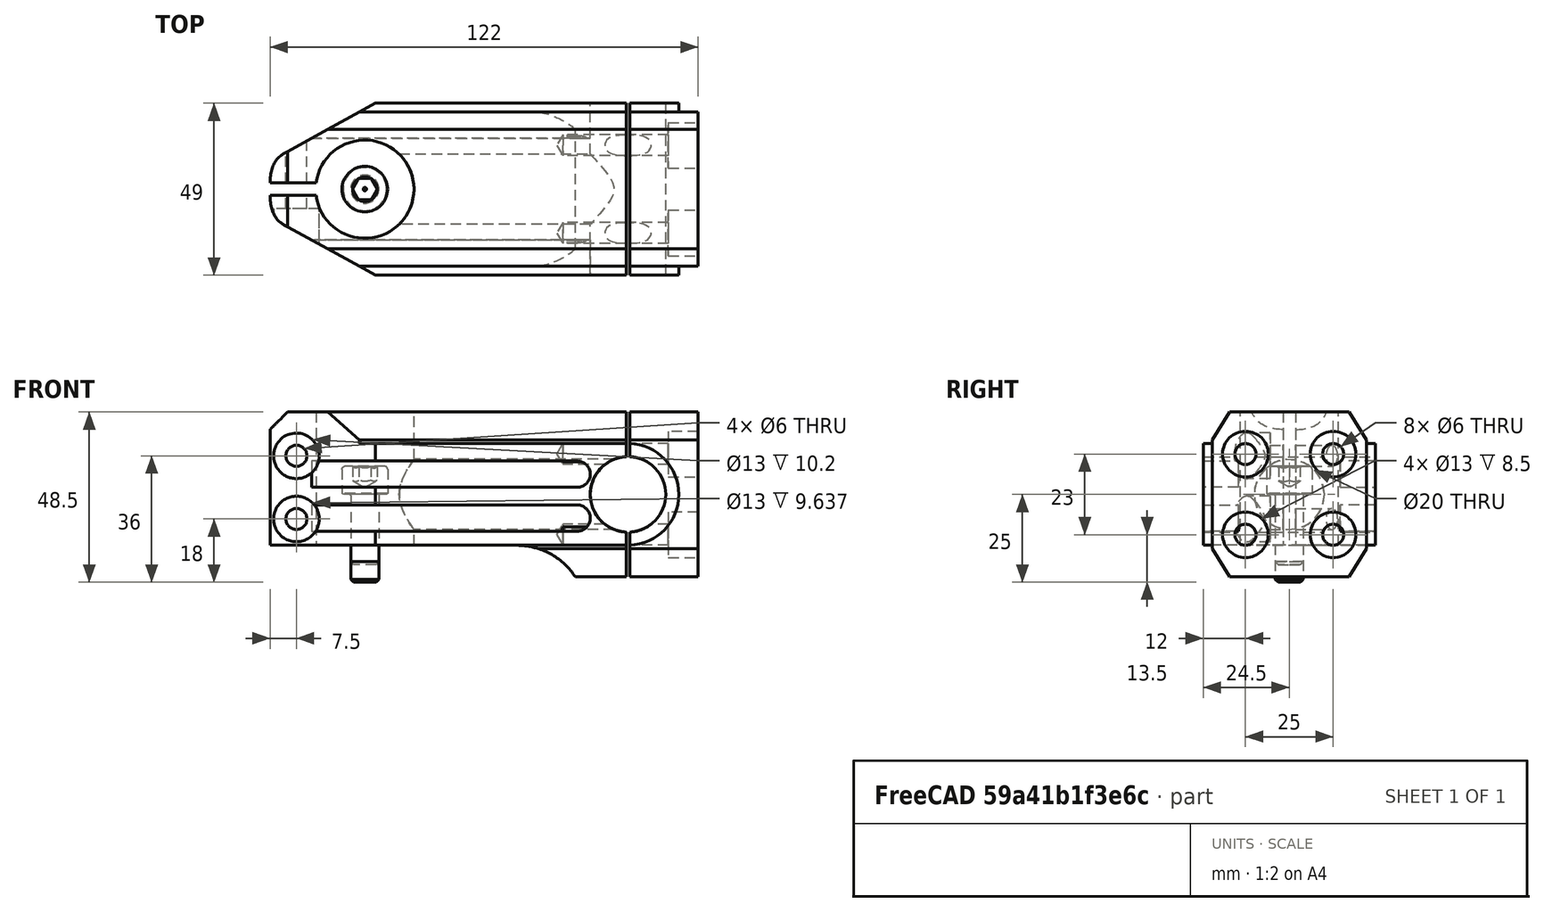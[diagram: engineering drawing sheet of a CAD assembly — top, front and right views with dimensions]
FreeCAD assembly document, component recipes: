
FREECAD ASSEMBLY — COMPONENT RECIPES ("Anchor")

This assembly document has 7 components, labeled P0..P6 below (a component is one placed body or linked part). 1 of them carries a construction recipe — the FreeCAD feature program that regenerates the part from scratch, quoted from this document or its linked companion documents; the rest are supplied as boundary geometry only. No exploded tour is included for this assembly.
COMPONENT P0 — geometry summary ("M8x20-Screw001"; no construction recipe available for this part):
  bounding box: 28.0 x 13.0 x 13.0 mm
  tessellated surface: 13,622 triangles
  volume: 1899 mm^3 (40% of its bounding box)
  symmetry: 6-fold rotationally symmetric about the y axis; mirror-symmetric across its x mid-plane, z mid-plane
COMPONENT P1 — geometry summary ("M8x20-Screw002"; no construction recipe available for this part):
  bounding box: 28.0 x 13.0 x 13.0 mm
  tessellated surface: 13,622 triangles
  volume: 1899 mm^3 (40% of its bounding box)
  symmetry: 6-fold rotationally symmetric about the y axis; mirror-symmetric across its x mid-plane, z mid-plane
COMPONENT P2 — geometry summary ("M8x25-Screw001"; no construction recipe available for this part):
  bounding box: 33.0 x 13.0 x 13.0 mm
  tessellated surface: 13,622 triangles
  volume: 2150 mm^3 (39% of its bounding box)
  symmetry: 6-fold rotationally symmetric about the x axis; mirror-symmetric across its y mid-plane, z mid-plane
COMPONENT P3 — geometry summary ("M8x25-Screw002"; no construction recipe available for this part):
  bounding box: 33.0 x 13.0 x 13.0 mm
  tessellated surface: 13,622 triangles
  volume: 2150 mm^3 (39% of its bounding box)
  symmetry: 6-fold rotationally symmetric about the x axis; mirror-symmetric across its y mid-plane, z mid-plane
COMPONENT P4 — geometry summary ("M8x25-Screw003"; no construction recipe available for this part):
  bounding box: 33.0 x 13.0 x 13.0 mm
  tessellated surface: 13,622 triangles
  volume: 2150 mm^3 (39% of its bounding box)
  symmetry: 6-fold rotationally symmetric about the x axis; mirror-symmetric across its y mid-plane, z mid-plane
COMPONENT P5 — geometry summary ("M8x25-Screw004"; no construction recipe available for this part):
  bounding box: 33.0 x 13.0 x 13.0 mm
  tessellated surface: 13,622 triangles
  volume: 2150 mm^3 (39% of its bounding box)
  symmetry: 6-fold rotationally symmetric about the x axis; mirror-symmetric across its y mid-plane, z mid-plane
COMPONENT P6 — recipe-attached ("Stem001", modeled in this document).
Construction recipe (the document's own serialized feature program — sketch geometry with constraints, then the solid features built on it; lengths are millimeters unless a unit is written):

FEATURE [Sketcher::SketchObject] Sketch
  ArcFitTolerance = 1e-06
  AttachmentSupport = -> [XZ_Plane001]
  FullyConstrained = true
  MakeInternals = false
  MapMode = 5
  Placement = pos=(0,0,0) rot=(1,0,0;1.5708rad)
  expr: Constraints[15] = <<VarSet>>.Size
  expr: Constraints[16] = <<VarSet>>.Size + 20 mm
  sketch-geometry (7):
    g0: Circle CenterX=75 CenterY=0 CenterZ=0 NormalX=0 NormalY=0 NormalZ=1 AngleXU=0 Radius=10.75
    g1: LineSegment StartX=0 StartY=23.5 StartZ=0 EndX=95 EndY=23.5 EndZ=0
    g2: LineSegment StartX=95 StartY=23.5 StartZ=0 EndX=95 EndY=-23.5 EndZ=0
    g3: LineSegment StartX=95 StartY=-23.5 StartZ=0 EndX=0 EndY=-23.5 EndZ=0
    g4: LineSegment StartX=0 StartY=-23.5 StartZ=0 EndX=-27 EndY=-23.5 EndZ=0
    g5: LineSegment StartX=-27 StartY=-23.5 StartZ=0 EndX=-27 EndY=23.5 EndZ=0
    g6: LineSegment StartX=-27 StartY=23.5 StartZ=0 EndX=0 EndY=23.5 EndZ=0
  constraints (20):
    c: Diameter(g0) = 21.5
    c: PointOnObject(g0,g-1)
    c: PointOnObject(g1,g-2)
    c: Horizontal(g1)
    c: Coincident(g1,g2)
    c: Coincident(g2,g3)
    c: PointOnObject(g3,g-2)
    c: Horizontal(g3)
    c: Coincident(g3,g4)
    c: Horizontal(g4)
    c: Coincident(g4,g5)
    c: Vertical(g5)
    c: Coincident(g5,g6)
    c: Coincident(g6,g1)
    c: Parallel(g6,g-1)
    c: Distance(g0,g-1) = 75
    c: Distance(g1) = 95
    c: Distance(g2) = 47
    c: Distance(g4) = 27
    c: Symmetric(g1,g2,g-1)
FEATURE [PartDesign::Pad] Pad
  Direction = (0,-1,2e-16)
  Length = 22
  Length2 = 10
  Placement = pos=(0,0,0) rot=(1,0,0;1.5708rad)
  Profile = -> Sketch
  ReferenceAxis = -> Sketch [N_Axis]
  Refine = true
  Suppressed = false
  Type = 0
FEATURE [PartDesign::Chamfer] Chamfer
  Angle = 45
  Base = -> Pad [Edge14,Edge15]
  BaseFeature = -> Pad
  ChamferType = 1
  FlipDirection = false
  Placement = pos=(0,0,0) rot=(1,0,0;1.5708rad)
  Refine = true
  Size = 8
  Size2 = 5
  SupportTransform = false
  Suppressed = false
  UseAllEdges = false
FEATURE [Sketcher::SketchObject] Sketch001
  ArcFitTolerance = 1e-06
  AttachmentSupport = -> [Chamfer]
  ExternalGeometry = -> [Chamfer]
  FullyConstrained = true
  MakeInternals = false
  MapMode = 5
  Placement = pos=(0,-22,0) rot=(1,0,0;1.5708rad)
  sketch-geometry (5):
    g0: ArcOfCircle CenterX=75 CenterY=4.9e-15 CenterZ=0 NormalX=0 NormalY=0 NormalZ=1 AngleXU=0 Radius=14.5 StartAngle=4.71239 EndAngle=7.85398
    g1: LineSegment StartX=75 StartY=14.5 StartZ=0 EndX=-27 EndY=14.5 EndZ=0
    g2: LineSegment StartX=75 StartY=-14.5 StartZ=0 EndX=-27 EndY=-14.5 EndZ=0
    g3: LineSegment StartX=-27 StartY=14.5 StartZ=0 EndX=-27 EndY=-14.5 EndZ=0
    g4: Circle CenterX=75 CenterY=4.9e-15 CenterZ=0 NormalX=0 NormalY=0 NormalZ=1 AngleXU=0 Radius=10.75
  constraints (14):
    c: Coincident(g0,g-4)
    c: Vertical(g0,g0)
    c: Vertical(g0,g0)
    c: Coincident(g0,g1)
    c: Coincident(g0,g2)
    c: Horizontal(g1)
    c: Horizontal(g2)
    c: Radius(g0) = 14.5
    c: Vertical(g3)
    c: Coincident(g1,g3)
    c: Coincident(g2,g3)
    c: Distance(g-1,g3) = 27
    c: Coincident(g4,g0)
    c: Equal(g4,g-4)
FEATURE [PartDesign::Pad] Pad001
  BaseFeature = -> Chamfer
  Direction = (0,-1,2e-16)
  Length = 2.5
  Length2 = 10
  Placement = pos=(0,0,0) rot=(1,0,0;1.5708rad)
  Profile = -> Sketch001
  ReferenceAxis = -> Sketch001 [N_Axis]
  Refine = true
  Suppressed = false
  Type = 0
FEATURE [Sketcher::SketchObject] Sketch002
  ArcFitTolerance = 1e-06
  AttachmentSupport = -> [Pad001]
  ExternalGeometry = -> [Pad001]
  FullyConstrained = true
  MakeInternals = false
  MapMode = 5
  Placement = pos=(0,-24.5,6.1e-15) rot=(1,0,0;1.5708rad)
  expr: Constraints[18] = VarSet.Size - 14.5 mm
  sketch-geometry (8):
    g0: LineSegment StartX=-27 StartY=9.5 StartZ=0 EndX=-27 EndY=2 EndZ=0
    g1: LineSegment StartX=-27 StartY=2 StartZ=0 EndX=60.5 EndY=2 EndZ=0
    g2: LineSegment StartX=60.5 StartY=9.5 StartZ=0 EndX=-27 EndY=9.5 EndZ=0
    g3: LineSegment StartX=-27 StartY=-3 StartZ=0 EndX=-27 EndY=-10.5 EndZ=0
    g4: LineSegment StartX=-27 StartY=-10.5 StartZ=0 EndX=60.5 EndY=-10.5 EndZ=0
    g5: LineSegment StartX=60.5 StartY=-3 StartZ=0 EndX=-27 EndY=-3 EndZ=0
    g6: ArcOfCircle CenterX=60.5 CenterY=5.75 CenterZ=0 NormalX=0 NormalY=0 NormalZ=1 AngleXU=0 Radius=3.75 StartAngle=4.71239 EndAngle=7.85398
    g7: ArcOfCircle CenterX=60.5 CenterY=-6.75 CenterZ=0 NormalX=0 NormalY=0 NormalZ=1 AngleXU=0 Radius=3.75 StartAngle=4.71239 EndAngle=7.85398
  constraints (22):
    c: Coincident(g0,g1)
    c: Coincident(g2,g0)
    c: Vertical(g0)
    c: Horizontal(g1)
    c: Horizontal(g2)
    c: PointOnObject(g0,g-3)
    c: Coincident(g3,g4)
    c: Coincident(g5,g3)
    c: Vertical(g3)
    c: Horizontal(g4)
    c: Horizontal(g5)
    c: PointOnObject(g3,g-3)
    c: Tangent(g6,g2) = -1.5708
    c: Tangent(g6,g1) = -1.5708
    c: Tangent(g7,g5) = -1.5708
    c: Tangent(g7,g4) = -1.5708
    c: Distance(g1,g2) = 7.5
    c: Distance(g-1,g1) = 2
    c: Distance(g6,g-2) = 60.5
    c: Vertical(g6,g7)
    c: Equal(g3,g0)
    c: Distance(g-1,g5) = 3
FEATURE [PartDesign::Pocket] Pocket
  BaseFeature = -> Pad001
  Direction = (0,1,-2e-16)
  Length = 10
  Length2 = 5
  Placement = pos=(0,0,0) rot=(1,0,0;1.5708rad)
  Profile = -> Sketch002
  ReferenceAxis = -> Sketch002 [N_Axis]
  Refine = true
  Suppressed = false
  Type = 0
FEATURE [Sketcher::SketchObject] Sketch003
  ArcFitTolerance = 1e-06
  AttachmentSupport = -> [Pocket]
  ExternalGeometry = -> [Pocket]
  FullyConstrained = true
  MakeInternals = false
  MapMode = 5
  Placement = pos=(0,-22,0) rot=(1,0,0;1.5708rad)
  expr: Constraints[9] = VarSet.Size - 15 mm
  sketch-geometry (5):
    g0: LineSegment StartX=43.2967 StartY=-14.5 StartZ=0 EndX=-27 EndY=-14.5 EndZ=0
    g1: LineSegment StartX=-27 StartY=-14.5 StartZ=0 EndX=-27 EndY=-23.5 EndZ=0
    g2: LineSegment StartX=-27 StartY=-23.5 StartZ=0 EndX=0 EndY=-23.5 EndZ=0
    g3: LineSegment StartX=0 StartY=-23.5 StartZ=0 EndX=60 EndY=-23.5 EndZ=0
    g4: ArcOfCircle CenterX=43.2967 CenterY=-34.5 CenterZ=0 NormalX=0 NormalY=0 NormalZ=1 AngleXU=0 Radius=20 StartAngle=0.582364 EndAngle=1.5708
  constraints (13):
    c: PointOnObject(g0,g-5)
    c: Coincident(g0,g-5)
    c: Coincident(g0,g1)
    c: Coincident(g1,g-4)
    c: Coincident(g1,g2)
    c: PointOnObject(g2,g-3)
    c: Coincident(g2,g3)
    c: PointOnObject(g3,g-3)
    c: PointOnObject(g2,g-2)
    c: DistanceX(g3,g3) = 60
    c: Coincident(g3,g4)
    c: Tangent(g4,g0) = -1.5708
    c: Radius(g4) = 20
FEATURE [PartDesign::Pocket] Pocket001
  BaseFeature = -> Pocket
  Direction = (0,1,-2e-16)
  Length = 5
  Length2 = 5
  Placement = pos=(0,0,0) rot=(1,0,0;1.5708rad)
  Profile = -> Sketch003
  ReferenceAxis = -> Sketch003 [N_Axis]
  Refine = true
  Suppressed = false
  Type = 1
FEATURE [Sketcher::SketchObject] Sketch004
  ArcFitTolerance = 1e-06
  AttachmentSupport = -> [Pocket001]
  ExternalGeometry = -> [Pocket001]
  FullyConstrained = true
  MakeInternals = false
  MapMode = 5
  Placement = pos=(0,1.13e-14,23.5) rot=(0,0,1;3.14159rad)
  sketch-geometry (10):
    g0: LineSegment StartX=-3 StartY=24.5 StartZ=0 EndX=27 EndY=24.5 EndZ=0
    g1: LineSegment StartX=27 StartY=24.5 StartZ=0 EndX=27 EndY=1.75 EndZ=0
    g2: LineSegment StartX=-3 StartY=24.5 StartZ=0 EndX=23 EndY=10.2 EndZ=0
    g3: LineSegment [constr] StartX=23 StartY=10.2 StartZ=0 EndX=27 EndY=8 EndZ=0
    g4: Circle [constr] CenterX=23 CenterY=10.2 CenterZ=0 NormalX=0 NormalY=0 NormalZ=1 AngleXU=0 Radius=1
    g5: Circle [constr] CenterX=27 CenterY=8 CenterZ=0 NormalX=0 NormalY=0 NormalZ=1 AngleXU=0 Radius=1
    g6: Circle [constr] CenterX=27 CenterY=1.75 CenterZ=0 NormalX=0 NormalY=0 NormalZ=1 AngleXU=0 Radius=1
    g7: BSplineCurve PolesCount=3 KnotsCount=2 Degree=2 IsPeriodic=0
    g8: GeomPoint [constr] X=23 Y=10.2 Z=0
    g9: GeomPoint [constr] X=27 Y=1.75 Z=0
  constraints (23):
    c: PointOnObject(g0,g-3)
    c: Coincident(g0,g-4)
    c: Coincident(g0,g1)
    c: PointOnObject(g1,g-6)
    c: DistanceY(g-6,g1) = 1.75
    c: Distance(g0,g-2) = 3
    c: Coincident(g0,g2)
    c: Distance(g2,g-2) = 23
    c: Coincident(g3,g2)
    c: PointOnObject(g3,g1)
    c: Parallel(g3,g2)
    c: DistanceY(g-6,g3) = 8
    c: Weight(g4) = 1
    c: Equal(g4,g5)
    c: Equal(g4,g6)
    c: InternalAlignment(g4,g7)
    c: InternalAlignment(g5,g7)
    c: InternalAlignment(g6,g7)
    c: InternalAlignment(g8,g7)
    c: InternalAlignment(g9,g7)
    c: Coincident(g4,g2)
    c: Coincident(g6,g1)
    c: Coincident(g5,g3)
FEATURE [PartDesign::Pocket] Pocket002
  BaseFeature = -> Pocket001
  Direction = (0,0,-1)
  Length = 5
  Length2 = 5
  Placement = pos=(0,0,0) rot=(1,0,0;1.5708rad)
  Profile = -> Sketch004
  ReferenceAxis = -> Sketch004 [N_Axis]
  Refine = true
  Suppressed = false
  Type = 1
FEATURE [PartDesign::Mirrored] Mirrored
  BaseFeature = -> Pocket002
  MirrorPlane = -> XZ_Plane001
  Placement = pos=(0,0,0) rot=(1,0,0;1.5708rad)
  Refine = true
  Suppressed = false
  TransformMode = 1
FEATURE [Sketcher::SketchObject] Sketch005
  ArcFitTolerance = 1e-06
  AttachmentSupport = -> [Mirrored]
  ExternalGeometry = -> [Mirrored]
  FullyConstrained = true
  MakeInternals = false
  MapMode = 5
  Placement = pos=(0,0,23.5) rot=(0,0,1;3.14159rad)
  sketch-geometry (4):
    g0: ArcOfCircle CenterX=0 CenterY=0 CenterZ=0 NormalX=0 NormalY=0 NormalZ=1 AngleXU=0 Radius=14 StartAngle=0.125328 EndAngle=6.15786
    g1: LineSegment StartX=27 StartY=1.75 StartZ=0 EndX=13.8902 EndY=1.75 EndZ=0
    g2: LineSegment StartX=27 StartY=-1.75 StartZ=0 EndX=13.8902 EndY=-1.75 EndZ=0
    g3: LineSegment StartX=27 StartY=1.75 StartZ=0 EndX=27 EndY=-1.75 EndZ=0
  constraints (10):
    c: Diameter(g0) = 28
    c: Coincident(g0,g-1)
    c: Coincident(g1,g-3)
    c: Horizontal(g1)
    c: Coincident(g2,g-3)
    c: Horizontal(g2)
    c: Coincident(g3,g1)
    c: Coincident(g3,g2)
    c: Coincident(g0,g2)
    c: Coincident(g0,g1)
FEATURE [PartDesign::Pocket] Pocket003
  BaseFeature = -> Mirrored
  Direction = (0,0,-1)
  Length = 5
  Length2 = 5
  Placement = pos=(0,0,0) rot=(1,0,0;1.5708rad)
  Profile = -> Sketch005
  ReferenceAxis = -> Sketch005 [N_Axis]
  Refine = true
  Suppressed = false
  Type = 1
FEATURE [Sketcher::SketchObject] Sketch006
  ArcFitTolerance = 1e-06
  AttachmentSupport = -> [XZ_Plane001]
  ExternalGeometry = -> [Pocket003]
  FullyConstrained = true
  MakeInternals = false
  MapMode = 5
  Placement = pos=(0,0,0) rot=(1,0,0;1.5708rad)
  sketch-geometry (3):
    g0: LineSegment StartX=-27 StartY=23.5 StartZ=0 EndX=-22 EndY=23.5 EndZ=0
    g1: LineSegment StartX=-22 StartY=23.5 StartZ=0 EndX=-27 EndY=18.5 EndZ=0
    g2: LineSegment StartX=-27 StartY=18.5 StartZ=0 EndX=-27 EndY=23.5 EndZ=0
  constraints (8):
    c: Coincident(g0,g-4)
    c: PointOnObject(g0,g-5)
    c: Coincident(g0,g1)
    c: PointOnObject(g1,g-3)
    c: Coincident(g1,g2)
    c: Coincident(g2,g0)
    c: DistanceX(g0,g0) = 5
    c: DistanceY(g2,g2) = 5
FEATURE [PartDesign::Pocket] Pocket004
  BaseFeature = -> Pocket003
  Direction = (0,1,-2e-16)
  Length = 5
  Length2 = 5
  Midplane = true
  Placement = pos=(0,0,0) rot=(1,0,0;1.5708rad)
  Profile = -> Sketch006
  ReferenceAxis = -> Sketch006 [N_Axis]
  Refine = true
  Suppressed = false
  Type = 1
FEATURE [Sketcher::SketchObject] Sketch007
  ArcFitTolerance = 1e-06
  AttachmentSupport = -> [Pocket004]
  FullyConstrained = true
  MakeInternals = false
  MapMode = 5
  Placement = pos=(95,0,0) rot=(0.707107,0,0.707107;3.14159rad)
  sketch-geometry (4):
    g0: Circle CenterX=11.5 CenterY=12.5 CenterZ=0 NormalX=0 NormalY=0 NormalZ=1 AngleXU=0 Radius=6.5
    g1: Circle CenterX=-11.5 CenterY=12.5 CenterZ=0 NormalX=0 NormalY=0 NormalZ=1 AngleXU=0 Radius=6.5
    g2: Circle CenterX=-11.5 CenterY=-12.5 CenterZ=0 NormalX=0 NormalY=0 NormalZ=1 AngleXU=0 Radius=6.5
    g3: Circle CenterX=11.5 CenterY=-12.5 CenterZ=0 NormalX=0 NormalY=0 NormalZ=1 AngleXU=0 Radius=6.5
  constraints (9):
    c: Symmetric(g0,g3,g-1)
    c: Symmetric(g1,g2,g-1)
    c: Symmetric(g2,g3,g-2)
    c: DistanceX(g1,g0) = 23
    c: DistanceY(g3,g0) = 25
    c: Equal(g0,g1)
    c: Equal(g1,g2)
    c: Equal(g2,g3)
    c: Diameter(g0) = 13
FEATURE [PartDesign::Pocket] Pocket005
  BaseFeature = -> Pocket004
  Direction = (-1,0,2e-16)
  Length = 8.5
  Length2 = 5
  Placement = pos=(0,0,0) rot=(1,0,0;1.5708rad)
  Profile = -> Sketch007
  ReferenceAxis = -> Sketch007 [N_Axis]
  Refine = true
  Suppressed = false
  Type = 0
FEATURE [PartDesign::Hole] Hole
  BaseFeature = -> Pocket005
  CustomThreadClearance = 0
  Depth = 30
  DepthType = 0
  Diameter = 6
  DrillForDepth = false
  DrillPoint = 1
  DrillPointAngle = 118
  HoleCutCountersinkAngle = 90
  HoleCutCustomValues = false
  HoleCutDepth = 0
  HoleCutDiameter = 6.1
  HoleCutType = 0
  ModelThread = false
  Placement = pos=(0,0,0) rot=(1,0,0;1.5708rad)
  Profile = -> Pocket005 [Face49,Face47,Face46,Face48]
  Refine = true
  Suppressed = false
  Tapered = false
  TaperedAngle = 90
  ThreadClass = 0
  ThreadDepth = 30
  ThreadDepthType = 0
  ThreadDirection = 0
  ThreadFit = 0
  ThreadSize = 0
  ThreadType = 0
  Threaded = false
  UseCustomThreadClearance = false
FEATURE [Sketcher::SketchObject] Sketch008
  ArcFitTolerance = 1e-06
  AttachmentSupport = -> [Hole]
  FullyConstrained = true
  MakeInternals = false
  MapMode = 5
  Placement = pos=(0,-14.5,4.8e-15) rot=(1,0,0;1.5708rad)
  sketch-geometry (2):
    g0: Circle CenterX=-19.5 CenterY=11 CenterZ=0 NormalX=0 NormalY=0 NormalZ=1 AngleXU=0 Radius=6.5
    g1: Circle CenterX=-19.5 CenterY=-7 CenterZ=0 NormalX=0 NormalY=0 NormalZ=1 AngleXU=0 Radius=6.5
  constraints (6):
    c: Vertical(g0,g1)
    c: Equal(g1,g0)
    c: DistanceY(g1,g-1) = 7
    c: Distance(g0,g-1) = 11
    c: DistanceX(g0,g-1) = 19.5
    c: Diameter(g0) = 13
FEATURE [PartDesign::Pocket] Pocket006
  BaseFeature = -> Hole
  Direction = (0,1,-2e-16)
  Length = 9
  Length2 = 7
  Placement = pos=(0,0,0) rot=(1,0,0;1.5708rad)
  Profile = -> Sketch008
  ReferenceAxis = -> Sketch008 [N_Axis]
  Refine = true
  Suppressed = false
  Type = 4
FEATURE [PartDesign::Hole] Hole001
  BaseFeature = -> Pocket006
  CustomThreadClearance = 0
  Depth = 25
  DepthType = 0
  Diameter = 6
  DrillForDepth = false
  DrillPoint = 1
  DrillPointAngle = 118
  HoleCutCountersinkAngle = 90
  HoleCutCustomValues = false
  HoleCutDepth = 0
  HoleCutDiameter = 6.1
  HoleCutType = 0
  ModelThread = false
  Placement = pos=(0,0,0) rot=(1,0,0;1.5708rad)
  Profile = -> Pocket006 [Face33,Face57]
  Refine = true
  Suppressed = false
  Tapered = false
  TaperedAngle = 90
  ThreadClass = 0
  ThreadDepth = 25
  ThreadDepthType = 0
  ThreadDirection = 0
  ThreadFit = 0
  ThreadSize = 0
  ThreadType = 0
  Threaded = false
  UseCustomThreadClearance = false
FEATURE [Sketcher::SketchObject] Sketch009
  ArcFitTolerance = 1e-06
  AttachmentSupport = -> [XZ_Plane001]
  ExternalGeometry = -> [Hole001]
  FullyConstrained = true
  MakeInternals = false
  MapMode = 5
  Placement = pos=(0,0,0) rot=(1,0,0;1.5708rad)
  expr: Constraints[10] = VarSet.Size + 0.5 mm
  expr: Constraints[9] = VarSet.Size - 0.5 mm
  sketch-geometry (4):
    g0: LineSegment StartX=74.5 StartY=23.5 StartZ=0 EndX=74.5 EndY=-23.5 EndZ=0
    g1: LineSegment StartX=74.5 StartY=-23.5 StartZ=0 EndX=75.5 EndY=-23.5 EndZ=0
    g2: LineSegment StartX=75.5 StartY=-23.5 StartZ=0 EndX=75.5 EndY=23.5 EndZ=0
    g3: LineSegment StartX=75.5 StartY=23.5 StartZ=0 EndX=74.5 EndY=23.5 EndZ=0
  constraints (12):
    c: Coincident(g0,g1)
    c: Coincident(g1,g2)
    c: Coincident(g2,g3)
    c: Coincident(g3,g0)
    c: Vertical(g0)
    c: Vertical(g2)
    c: Horizontal(g1)
    c: Horizontal(g3)
    c: PointOnObject(g0,g-3)
    c: Distance(g-2,g0) = 74.5
    c: Distance(g-2,g2) = 75.5
    c: PointOnObject(g0,g-4)
FEATURE [PartDesign::Pocket] Pocket007
  BaseFeature = -> Hole001
  Direction = (0,1,-2e-16)
  Length = 5
  Length2 = 5
  Midplane = true
  Placement = pos=(0,0,0) rot=(1,0,0;1.5708rad)
  Profile = -> Sketch009
  ReferenceAxis = -> Sketch009 [N_Axis]
  Refine = true
  Suppressed = false
  Type = 1
FEATURE [Sketcher::SketchObject] Sketch010
  ArcFitTolerance = 1e-06
  AttachmentSupport = -> [YZ_Plane001]
  FullyConstrained = true
  MakeInternals = false
  MapMode = 5
  Placement = pos=(0,0,0) rot=(0.57735,0.57735,0.57735;2.0944rad)
  sketch-geometry (1):
    g0: Circle CenterX=0 CenterY=0 CenterZ=0 NormalX=0 NormalY=0 NormalZ=1 AngleXU=0 Radius=10
  constraints (2):
    c: Diameter(g0) = 20
    c: Coincident(g0,g-1)
FEATURE [PartDesign::Pocket] Pocket008
  BaseFeature = -> Pocket007
  Direction = (-1,0,0)
  Length = 0
  Length2 = 5
  Placement = pos=(0,0,0) rot=(1,0,0;1.5708rad)
  Profile = -> Sketch010
  ReferenceAxis = -> Sketch010 [N_Axis]
  Refine = true
  Suppressed = false
  Type = 3
  UpToFace = -> Pocket007 [Face18]
FEATURE [PartDesign::Body] Body  label="Stem"
  AllowCompound = true
  Group = -> [Sketch,Pad,Chamfer,Sketch001,Pad001,Sketch002,Pocket,Sketch003,Pocket001,Sketch004,Pocket002,Mirrored,Sketch005,Pocket003,Sketch006,Pocket004,Sketch007,Pocket005,Hole,Sketch008,Pocket006,Hole001,Sketch009,Pocket007,Sketch010,Pocket008]
  Origin = -> Origin001
  Tip = -> Pocket008
PROVENANCE & LICENSES
A FreeCAD (.FCStd) document from a public repository crawl; recipes are the document's own serialized feature recipes (and, for linked parts, companion documents' recipes).
License: as declared in the source repository (recorded in the dataset sidecar).
